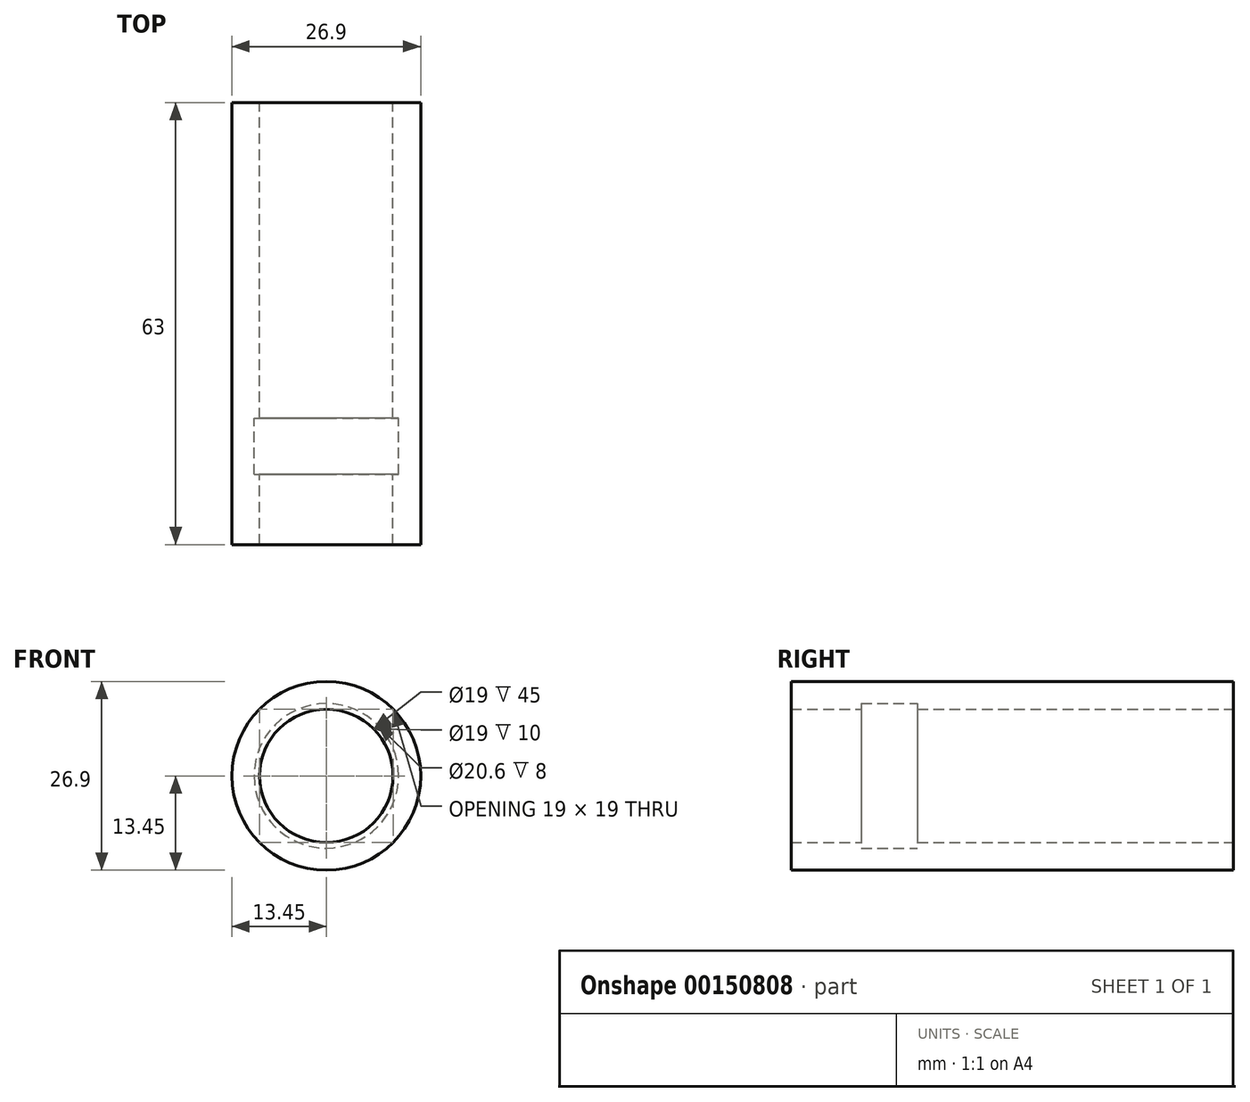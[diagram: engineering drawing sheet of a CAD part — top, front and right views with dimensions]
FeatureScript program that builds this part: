
annotation { "Feature Type Name" : "Feature", "Feature Type Description" : "" }
export const myFeature = defineFeature(function(context is Context, id is Id, definition is map)
    precondition{}
    {
        {
            var Q0;
            Q0=qCreatedBy(makeId("Front.planeOp"),FACE);
            var sketch = newSketch(context, id + "F0", { "sketchPlane" : qUnion([Q0])});
            skCircle(sketch, "E0", {"center": v(0, 0) * mm, "radius": 13.45 * mm});
            skCircle(sketch, "E1", {"center": v(0, 0) * mm, "radius": 9.5 * mm});
            skSolve(sketch);
        }
        {
            var Q0;
            Q0=makeQuery(id+"F0.imprint","IMPRINT",FACE,{"disambiguationData":[TD([[makeQuery(id+"F0.imprint","IMPRINT",EDGE,{"derivedFrom":sQuery(id+"F0.wireOp",EDGE,"E0")}),1.0]])]});
            extrude(context, id + "F1", {"entities" : qUnion([Q0]), "depth" : 63 * mm});
        }
        {
            var Q0;
            Q0=qCreatedBy(makeId("Right.planeOp"),FACE);
            var sketch = newSketch(context, id + "F2", { "sketchPlane" : qUnion([Q0])});
            skLineSegment(sketch, "E2", {"start": v(0, 0) * mm, "end": v(-63, 0) * mm, "construction": true});
            skLineSegment(sketch, "E3.0", {"start": v(-63, -9.5) * mm, "end": v(-63, 9.5) * mm, "construction": true});
            skLineSegment(sketch, "E4", {"start": v(-63, 9.5) * mm, "end": v(-53, 9.5) * mm, "construction": true});
            skLineSegment(sketch, "E5", {"start": v(-45, 9.5) * mm, "end": v(-53, 9.5) * mm});
            skLineSegment(sketch, "E6", {"start": v(-63, 9.5) * mm, "end": v(-63, 11.71) * mm, "construction": true});
            skLineSegment(sketch, "E7", {"start": v(-45, 9.5) * mm, "end": v(-45, 10.3) * mm});
            skLineSegment(sketch, "E8", {"start": v(-45, 10.3) * mm, "end": v(-53, 10.3) * mm});
            skLineSegment(sketch, "E9", {"start": v(-53, 10.3) * mm, "end": v(-53, 9.5) * mm});
            skLineSegment(sketch, "E10", {"start": v(-53, 10.3) * mm, "end": v(-63, 10.3) * mm, "construction": true});
            skPoint(sketch, "E10.endSnap0", {"position": v(-63, 10.6) * mm});
            skLineSegment(sketch, "E11", {"start": v(-63, 9.5) * mm, "end": v(-63, 10.3) * mm, "construction": true});
            skSolve(sketch);
        }
        {
            var Q0;
            Q0=qSketchRegion(id+"F2",true);
            var Q1;
            Q1=sQuery(id+"F2.wireOp",EDGE,"E2");
            revolve(context, id + "F3", {"operationType" : NewBodyOperationType.REMOVE, "entities" : qUnion([Q0]), "axis" : qUnion([Q1]), "revolveType" : RevolveType.FULL});
        }
    });
